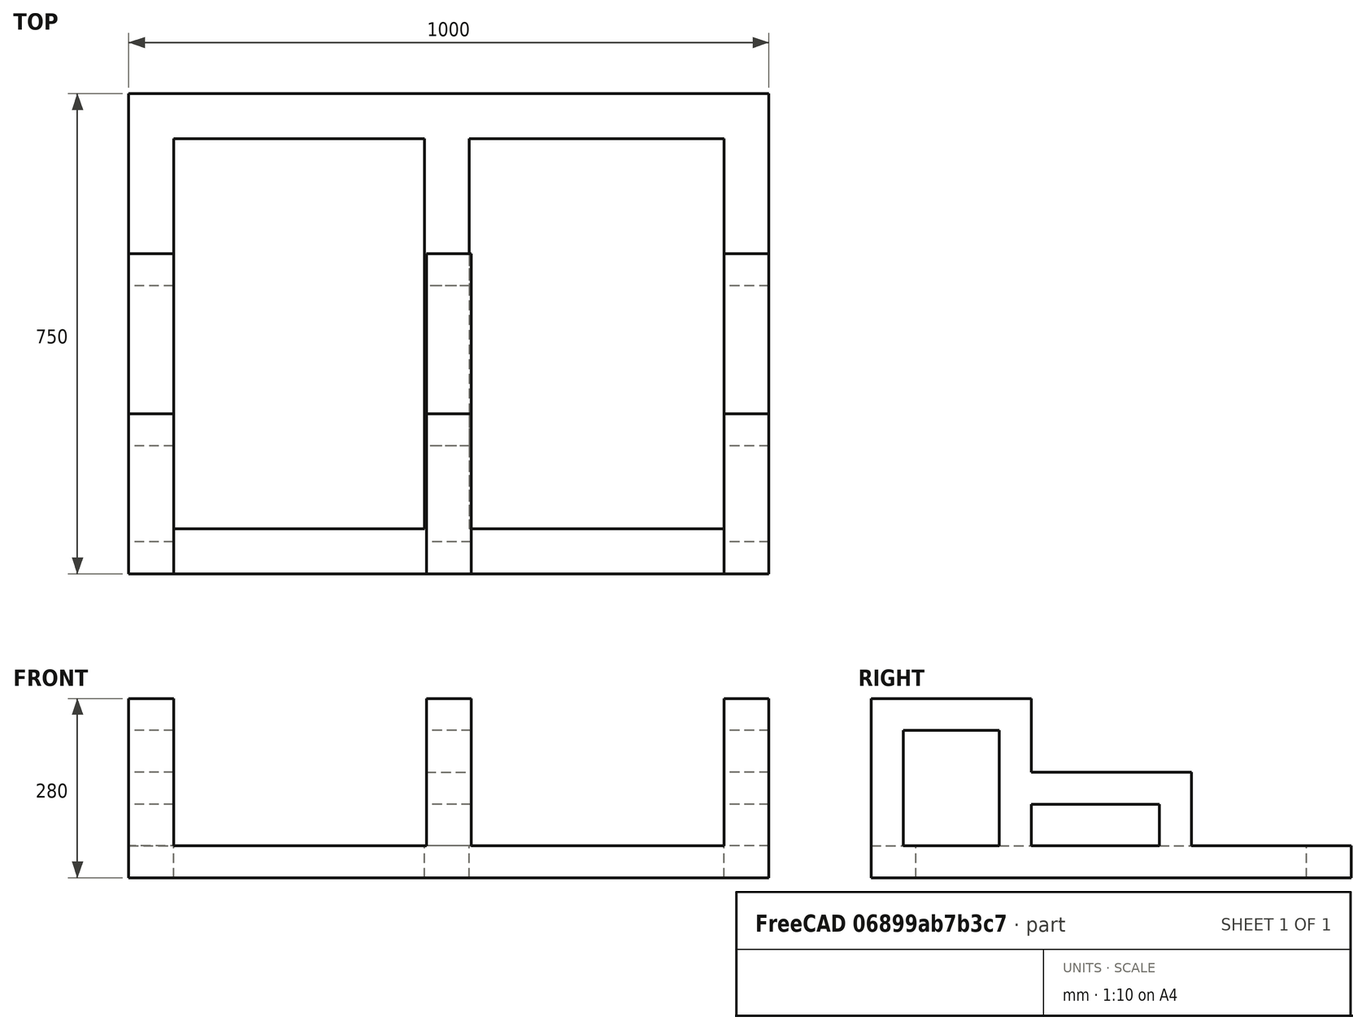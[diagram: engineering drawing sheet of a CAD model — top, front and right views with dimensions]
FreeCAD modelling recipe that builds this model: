
FCSTD DOCUMENT  (FreeCAD 0.18R16131 (Git))
Label: escalier
License: All rights reserved
LicenseURL: http://en.wikipedia.org/wiki/All_rights_reserved
objects: TechDraw::DrawViewDimension×10, Sketcher::SketchObject×5, PartDesign::Pad×5, PartDesign::LinearPattern×4, TechDraw::DrawViewPart×3, PartDesign::Plane×2, TechDraw::DrawViewAnnotation×2, PartDesign::Mirrored×1, PartDesign::MultiTransform×1, PartDesign::Body×1, TechDraw::DrawSVGTemplate×1, TechDraw::DrawPage×1
note: 24 computed .brp shape members not serialized (recipe doc carries the construction recipe); baked Part::Feature solids carry a one-line shape summary decoded from their .brp

FEATURE [Sketcher::SketchObject] Sketch
  MapMode = 5
  Support = -> [XY_Plane]
  sketch-geometry (13):
    g0: LineSegment StartX=0 StartY=0 StartZ=0 EndX=1000 EndY=0 EndZ=0
    g1: LineSegment StartX=1000 StartY=0 StartZ=0 EndX=1000 EndY=750 EndZ=0
    g2: LineSegment StartX=1000 StartY=750 StartZ=0 EndX=0 EndY=750 EndZ=0
    g3: LineSegment StartX=0 StartY=750 StartZ=0 EndX=0 EndY=0 EndZ=0
    g4: LineSegment StartX=70 StartY=680 StartZ=0 EndX=462.088 EndY=680 EndZ=0
    g5: LineSegment StartX=930 StartY=680 StartZ=0 EndX=930 EndY=70 EndZ=0
    g6: LineSegment StartX=930 StartY=70 StartZ=0 EndX=532.088 EndY=70 EndZ=0
    g7: LineSegment StartX=70 StartY=70 StartZ=0 EndX=70 EndY=680 EndZ=0
    g8: LineSegment [constr] StartX=499.248 StartY=720 StartZ=0 EndX=499.248 EndY=-65.6651 EndZ=0
    g9: LineSegment StartX=462.088 StartY=680 StartZ=0 EndX=462.088 EndY=70 EndZ=0
    g10: LineSegment StartX=532.088 StartY=680 StartZ=0 EndX=532.088 EndY=70 EndZ=0
    g11: LineSegment StartX=462.088 StartY=70 StartZ=0 EndX=70 EndY=70 EndZ=0
    g12: LineSegment StartX=532.088 StartY=680 StartZ=0 EndX=930 EndY=680 EndZ=0
  constraints (35):
    c: PointOnObject(g0,g-1)
    c: Coincident(g0,g1)
    c: Vertical(g1)
    c: Coincident(g2,g3)
    c: Coincident(g3,g0)
    c: Vertical(g3)
    c: Coincident(g12,g5)
    c: Coincident(g5,g6)
    c: Coincident(g11,g7)
    c: Coincident(g7,g4)
    c: Horizontal(g6)
    c: Vertical(g5)
    c: Vertical(g7)
    c: DistanceX(g0,g0) = 1000
    c: DistanceY(g0,g1) = 750
    c: Coincident(g0,g-1)
    c: DistanceY(g0,g11) = 70
    c: DistanceX(g0,g11) = 70
    c: DistanceX(g12,g1) = 70
    c: Vertical(g8)
    c: PointOnObject(g9,g6)
    c: Vertical(g9)
    c: Vertical(g10)
    c: PointOnObject(g10,g4)
    c: Horizontal(g4)
    c: DistanceY(g4,g2) = 70
    c: Horizontal(g2)
    c: Coincident(g2,g1)
    c: Coincident(g6,g10)
    c: Tangent(g6,g11)
    c: PointOnObject(g11,g9)
    c: Coincident(g4,g9)
    c: Tangent(g4,g12)
    c: PointOnObject(g12,g10)
    c: DistanceX(g4,g10) = 70
FEATURE [PartDesign::Pad] Pad
  Length = 50
  Length2 = 100
  Profile = -> Sketch
  Type = 0
FEATURE [Sketcher::SketchObject] Sketch001  label="pieds"
  AttachmentOffset = pos=(0,0,50) rot=(0,0,1;0rad)
  ExternalGeometry = -> [Sketch]
  MapMode = 5
  Placement = pos=(0,0,50) rot=(0,0,1;0rad)
  Support = -> [XY_Plane]
  sketch-geometry (6):
    g0: LineSegment StartX=0 StartY=0 StartZ=0 EndX=70 EndY=0 EndZ=0
    g1: LineSegment StartX=70 StartY=0 StartZ=0 EndX=70 EndY=50 EndZ=0
    g2: LineSegment StartX=70 StartY=50 StartZ=0 EndX=0 EndY=50 EndZ=0
    g3: LineSegment StartX=0 StartY=50 StartZ=0 EndX=0 EndY=0 EndZ=0
    g4: LineSegment [constr] StartX=500 StartY=750 StartZ=0 EndX=500 EndY=-340.786 EndZ=0
    g5: LineSegment [constr] StartX=-164.15 StartY=125 StartZ=0 EndX=1581.27 EndY=125 EndZ=0
  constraints (15):
    c: Coincident(g0,g1)
    c: Coincident(g1,g2)
    c: Coincident(g2,g3)
    c: Coincident(g3,g0)
    c: Horizontal(g0)
    c: Horizontal(g2)
    c: Vertical(g1)
    c: Vertical(g3)
    c: Coincident(g0,g-1)
    c: DistanceX(g2,g2) = 70
    c: DistanceY(g1,g1) = 50
    c: Vertical(g4)
    c: Symmetric(g-3,g-4,g4)
    c: Horizontal(g5)
    c: DistanceY(g-4,g5) = 125
FEATURE [PartDesign::Pad] Pad001  label="pieds1"
  BaseFeature = -> Pad
  Length = 180
  Length2 = 100
  Profile = -> Sketch001
  Type = 0
FEATURE [PartDesign::Mirrored] Mirrored001
  MirrorPlane = -> Sketch001 [Axis1]
FEATURE [Sketcher::SketchObject] Sketch002
  AttachmentOffset = pos=(0,0,50) rot=(0,0,1;0rad)
  ExternalGeometry = -> [Sketch]
  MapMode = 5
  Placement = pos=(0,0,50) rot=(0,0,1;0rad)
  Support = -> [XY_Plane]
  sketch-geometry (5):
    g0: LineSegment StartX=0 StartY=500 StartZ=0 EndX=70 EndY=500 EndZ=0
    g1: LineSegment StartX=70 StartY=500 StartZ=0 EndX=70 EndY=450 EndZ=0
    g2: LineSegment StartX=70 StartY=450 StartZ=0 EndX=0 EndY=450 EndZ=0
    g3: LineSegment StartX=0 StartY=450 StartZ=0 EndX=0 EndY=500 EndZ=0
    g4: LineSegment [constr] StartX=500 StartY=750 StartZ=0 EndX=500 EndY=-340.46 EndZ=0
  constraints (14):
    c: Coincident(g0,g1)
    c: Coincident(g1,g2)
    c: Coincident(g2,g3)
    c: Coincident(g3,g0)
    c: Horizontal(g0)
    c: Horizontal(g2)
    c: Vertical(g1)
    c: Vertical(g3)
    c: DistanceX(g0,g0) = 70
    c: DistanceY(g1,g1) = 50
    c: DistanceY(g-1,g0) = 500
    c: Vertical(g4)
    c: Symmetric(g-4,g-3,g4)
    c: PointOnObject(g2,g-4)
FEATURE [PartDesign::Plane] DatumPlane
  Length = 1185.23
  MapMode = 5
  Placement = pos=(0,0,230) rot=(0,0,1;0rad)
  ResizeMode = 0
  Width = 935.226
FEATURE [Sketcher::SketchObject] Sketch003
  MapMode = 5
  Placement = pos=(0,0,230) rot=(0,0,1;0rad)
  Support = -> [DatumPlane]
  sketch-geometry (5):
    g0: LineSegment StartX=0 StartY=250 StartZ=0 EndX=70 EndY=250 EndZ=0
    g1: LineSegment StartX=70 StartY=250 StartZ=0 EndX=70 EndY=0 EndZ=0
    g2: LineSegment StartX=70 StartY=0 StartZ=0 EndX=0 EndY=0 EndZ=0
    g3: LineSegment StartX=0 StartY=0 StartZ=0 EndX=0 EndY=250 EndZ=0
    g4: LineSegment [constr] StartX=500 StartY=720 StartZ=0 EndX=500 EndY=-285.794 EndZ=0
  constraints (12):
    c: Coincident(g0,g1)
    c: Coincident(g1,g2)
    c: Coincident(g2,g3)
    c: Coincident(g3,g0)
    c: Horizontal(g0)
    c: Horizontal(g2)
    c: Vertical(g1)
    c: Vertical(g3)
    c: Vertical(g4)
    c: Coincident(g-1,g2)
    c: DistanceX(g0,g0) = 70
    c: DistanceY(g3,g3) = 250
FEATURE [PartDesign::LinearPattern] LinearPattern
  Direction = -> Sketch001 [H_Axis]
  Length = 930
  Occurrences = 3
FEATURE [PartDesign::MultiTransform] MultiTransform
  BaseFeature = -> Pad001
  Originals = -> [Pad001]
  Transformations = -> [Mirrored001,LinearPattern]
FEATURE [PartDesign::Pad] Pad002  label="pieds2"
  BaseFeature = -> MultiTransform
  Length = 65
  Length2 = 100
  Profile = -> Sketch002
  Type = 0
FEATURE [PartDesign::Pad] Pad003  label="Hori lame 1"
  BaseFeature = -> Pad002
  Length = 50
  Length2 = 100
  Profile = -> Sketch003
  Type = 0
FEATURE [PartDesign::Plane] DatumPlane001
  Length = 1185.23
  MapMode = 5
  Placement = pos=(0,0,115) rot=(0,0,1;0rad)
  ResizeMode = 0
  Support = -> [Pad003]
  Width = 935.226
FEATURE [PartDesign::LinearPattern] LinearPattern001
  BaseFeature = -> Pad003
  Direction = -> Sketch002 [H_Axis]
  Length = 930
  Occurrences = 3
  Originals = -> [Pad002]
FEATURE [PartDesign::LinearPattern] LinearPattern002  label="Hori Lame rep"
  BaseFeature = -> LinearPattern001
  Direction = -> Sketch003 [H_Axis]
  Length = 930
  Occurrences = 3
  Originals = -> [Pad003]
FEATURE [Sketcher::SketchObject] Sketch004
  MapMode = 5
  Placement = pos=(0,0,115) rot=(0,0,1;0rad)
  Support = -> [DatumPlane001]
  sketch-geometry (4):
    g0: LineSegment StartX=0 StartY=500 StartZ=0 EndX=70 EndY=500 EndZ=0
    g1: LineSegment StartX=70 StartY=500 StartZ=0 EndX=70 EndY=250 EndZ=0
    g2: LineSegment StartX=70 StartY=250 StartZ=0 EndX=0 EndY=250 EndZ=0
    g3: LineSegment StartX=0 StartY=250 StartZ=0 EndX=0 EndY=500 EndZ=0
  constraints (12):
    c: Coincident(g2,g3)
    c: Coincident(g0,g3)
    c: Coincident(g1,g2)
    c: Coincident(g0,g1)
    c: DistanceX(g0,g0) = 70
    c: DistanceY(g2,g0) = 250
    c: Vertical(g3)
    c: Vertical(g1)
    c: Horizontal(g0)
    c: Horizontal(g2)
    c: PointOnObject(g0,g-2)
    c: DistanceY(g-1,g2) = 250
FEATURE [PartDesign::Pad] Pad004  label="Hori lame 2 pad"
  BaseFeature = -> LinearPattern002
  Length = 50
  Length2 = 100
  Profile = -> Sketch004
  Type = 0
FEATURE [PartDesign::LinearPattern] LinearPattern003  label="Hori Lame 2 rep"
  BaseFeature = -> Pad004
  Direction = -> Sketch004 [H_Axis]
  Length = 930
  Occurrences = 3
  Originals = -> [Pad004]
FEATURE [PartDesign::Body] Body
  Group = -> [Sketch,Pad,Sketch001,Pad001,MultiTransform,Mirrored001,Sketch002,Pad002,DatumPlane,Sketch003,Pad003,DatumPlane001,LinearPattern,LinearPattern001,LinearPattern002,Sketch004,Pad004,LinearPattern003]
  Origin = -> Origin
  Tip = -> LinearPattern003
FEATURE [TechDraw::DrawSVGTemplate] Template
  EditableTexts = Designed_by_Name=Yvan; Drawing_number=Drawing number; FC-Date=03/09/2020; FC-SC=Scale; FC-SH=Sheet; FC-Title=Escalier terrasse; Subtitle=Subtitle; Weight=Weight
  Height = 210
  Orientation = 1
  Width = 297
FEATURE [TechDraw::DrawViewPart] View
  CoarseView = false
  Direction = (0.446,0.837,0.317)
  Focus = 100
  HardHidden = false
  IsoCount = 0
  IsoHidden = false
  IsoVisible = false
  LockPosition = false
  Perspective = false
  Rotation = 0
  Scale = 0.08
  ScaleType = 0
  SeamHidden = false
  SeamVisible = false
  SmoothHidden = false
  SmoothVisible = false
  Source = -> [Body]
  X = 225.067
  Y = 162.916
FEATURE [TechDraw::DrawViewPart] View001
  CoarseView = false
  Direction = (1,0,0)
  Focus = 100
  HardHidden = false
  IsoCount = 0
  IsoHidden = false
  IsoVisible = false
  LockPosition = false
  Perspective = false
  Rotation = 0
  Scale = 0.12
  ScaleType = 0
  SeamHidden = false
  SeamVisible = false
  SmoothHidden = false
  SmoothVisible = false
  Source = -> [Body]
  X = 63.8866
  Y = 171.162
FEATURE [TechDraw::DrawViewPart] View003
  CoarseView = false
  Direction = (0,0,1)
  Focus = 100
  HardHidden = false
  IsoCount = 0
  IsoHidden = false
  IsoVisible = false
  LockPosition = false
  Perspective = false
  Rotation = 90
  Scale = 0.12
  ScaleType = 0
  SeamHidden = true
  SeamVisible = false
  SmoothHidden = false
  SmoothVisible = false
  Source = -> [Body]
  X = 64.5103
  Y = 80.3579
FEATURE [TechDraw::DrawViewDimension] Dimension
  Arbitrary = false
  FormatSpec = %.2f
  LockPosition = false
  MeasureType = 1
  OverTolerance = 0
  References2D = -> [View003]
  Rotation = 0
  ScaleType = 0
  Type = 2
  UnderTolerance = 0
  X = 65.0279
  Y = -0.216974
FEATURE [TechDraw::DrawViewDimension] Dimension003
  Arbitrary = false
  FormatSpec = %.2f
  LockPosition = false
  MeasureType = 1
  OverTolerance = 0
  References2D = -> [View001]
  Rotation = 0
  ScaleType = 0
  Type = 1
  UnderTolerance = 0
  X = -29.4604
  Y = 25.5571
FEATURE [TechDraw::DrawViewDimension] Dimension007
  Arbitrary = false
  FormatSpec = %.2f
  LockPosition = false
  MeasureType = 1
  OverTolerance = 0
  References2D = -> [View001]
  Rotation = 0
  ScaleType = 0
  Type = 2
  UnderTolerance = 0
  X = 25.3528
  Y = 4.72933
FEATURE [TechDraw::DrawViewDimension] Dimension008
  Arbitrary = false
  FormatSpec = %.2f
  LockPosition = false
  MeasureType = 1
  OverTolerance = 0
  References2D = -> [View001]
  Rotation = 0
  ScaleType = 0
  Type = 2
  UnderTolerance = 0
  X = 33.9083
  Y = 22.5841
FEATURE [TechDraw::DrawViewDimension] Dimension012
  Arbitrary = false
  FormatSpec = %.1f
  LockPosition = false
  MeasureType = 1
  OverTolerance = 0
  References2D = -> [View003]
  Rotation = 0
  ScaleType = 0
  Type = 2
  UnderTolerance = 0
  X = -52.1096
  Y = 0.042679
FEATURE [TechDraw::DrawViewAnnotation] Annotation
  Font = MS Shell Dlg 2
  LineSpace = 80
  LockPosition = false
  MaxWidth = -1
  Rotation = 0
  ScaleType = 0
  Text = Horizontal | 6 * 25 | 2 * 75 | 1 * 61
  TextSize = 8
  TextStyle = 0
  X = 187.831
  Y = 112.923
FEATURE [TechDraw::DrawViewAnnotation] Annotation001
  Font = MS Shell Dlg 2
  LineSpace = 80
  LockPosition = false
  MaxWidth = -1
  Rotation = 0
  ScaleType = 0
  Text = Vertical | 6 * 18 | 3 * 8
  TextSize = 8
  TextStyle = 0
  X = 226.879
  Y = 116.318
FEATURE [TechDraw::DrawViewDimension] Dimension019
  Arbitrary = false
  FormatSpec = %.2f
  LockPosition = false
  MeasureType = 1
  OverTolerance = 0
  References2D = -> [View001]
  Rotation = 0
  ScaleType = 0
  Type = 1
  UnderTolerance = 0
  X = 2.32472
  Y = 25.4642
FEATURE [TechDraw::DrawViewDimension] Dimension020
  Arbitrary = false
  FormatSpec = %.2f
  LockPosition = false
  MeasureType = 1
  OverTolerance = 0
  References2D = -> [View001]
  Rotation = 0
  ScaleType = 0
  Type = 1
  UnderTolerance = 0
  X = -31.7085
  Y = -19.0657
FEATURE [TechDraw::DrawViewDimension] Dimension021
  Arbitrary = false
  FormatSpec = %.2f
  LockPosition = false
  MeasureType = 1
  OverTolerance = 0
  References2D = -> [View001]
  Rotation = 0
  ScaleType = 0
  Type = 1
  UnderTolerance = 0
  X = -11.0258
  Y = -22.1653
FEATURE [TechDraw::DrawViewDimension] Dimension022
  Arbitrary = false
  FormatSpec = %.2f
  LockPosition = false
  MeasureType = 1
  OverTolerance = 0
  References2D = -> [View003]
  Rotation = 0
  ScaleType = 0
  Type = 1
  UnderTolerance = 0
  X = 0.774908
  Y = -63.2236
FEATURE [TechDraw::DrawViewDimension] Dimension023
  Arbitrary = false
  FormatSpec = %.2f
  LockPosition = false
  MeasureType = 1
  OverTolerance = 0
  References2D = -> [View003]
  Rotation = 0
  ScaleType = 0
  Type = 1
  UnderTolerance = 0
  X = -3.87454
  Y = -9.75498
FEATURE [TechDraw::DrawPage] Page
  KeepUpdated = true
  ProjectionType = 0
  Template = -> Template
  Views = -> [View,View001,View003,Dimension,Dimension003,Dimension007,Dimension008,Dimension012,Annotation,Annotation001,Dimension019,Dimension020,Dimension021,Dimension022,Dimension023]
